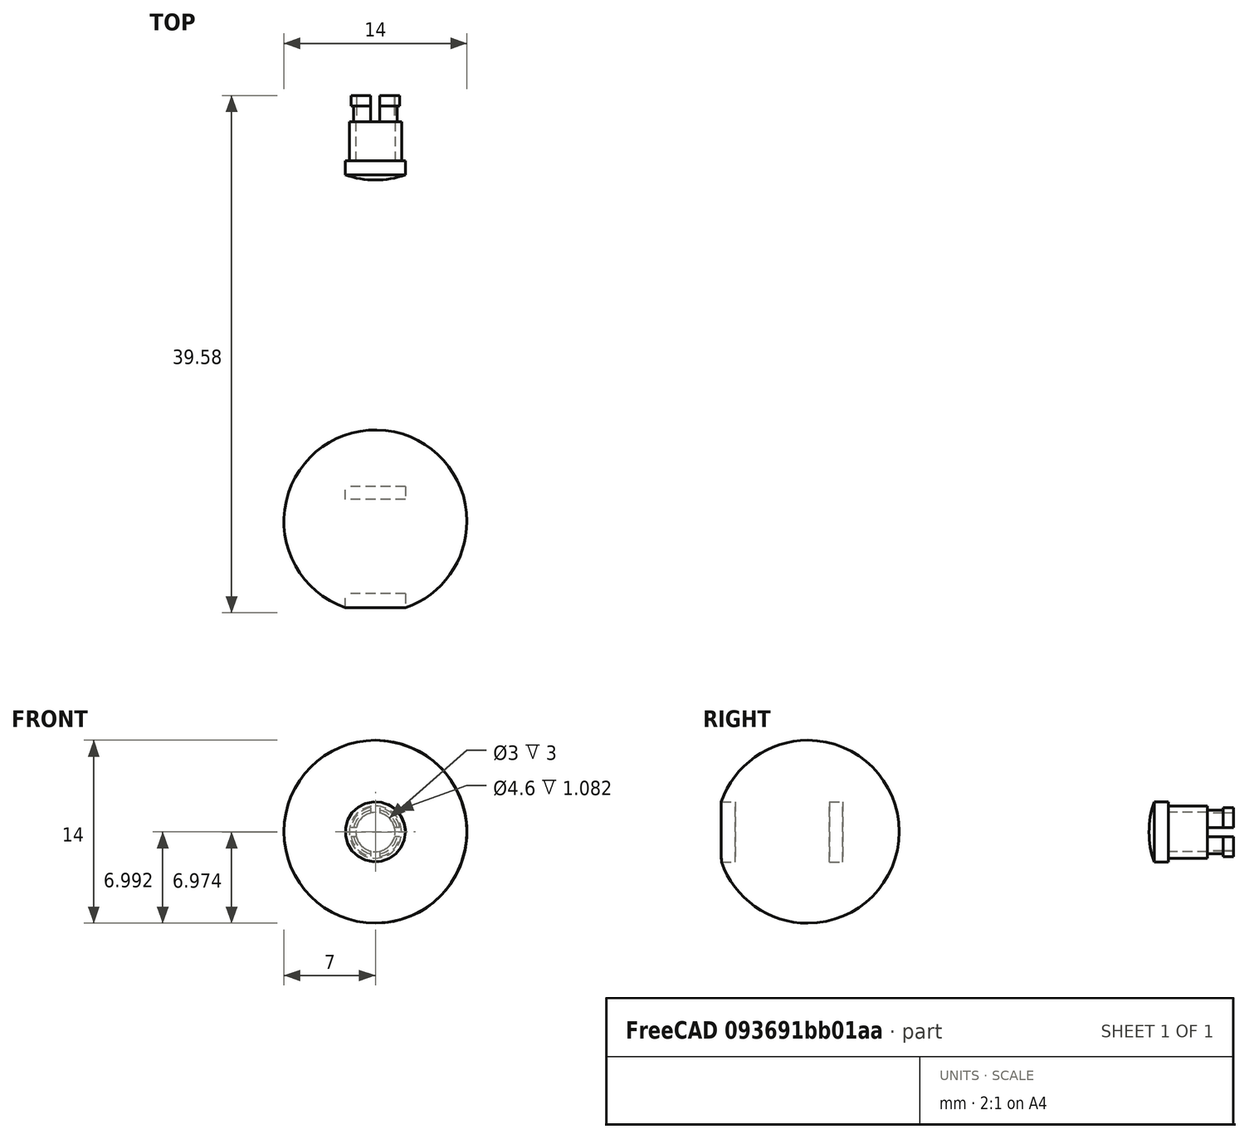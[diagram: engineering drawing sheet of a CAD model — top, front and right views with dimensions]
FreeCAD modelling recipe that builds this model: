
FCSTD DOCUMENT  (FreeCAD 0.21R33771 (Git))
Label: led_lens
License: All rights reserved
LicenseURL: http://en.wikipedia.org/wiki/All_rights_reserved
objects: Part::Cut×5, Part::Box×4, Part::FeaturePython×3, Part::Cylinder×2, Part::MultiFuse×2, Part::Feature×1, Part::Fuse×1, Part::Sphere×1, Part::Common×1
note: 20 computed .brp shape members not serialized (recipe doc carries the construction recipe); baked Part::Feature solids carry a one-line shape summary decoded from their .brp

FEATURE [Part::Feature] Part__Feature468  label="Document"
  Placement = pos=(0,12.544,0) rot=(0,0,1;0rad)
  shape: bbox 3.85 x 5.412 x 4.122 mm, 7 faces, 0 solids (baked)
FEATURE [Part::Cylinder] Cylinder
  Angle = 360
  AttacherType = Attacher::AttachEngine3D
  FirstAngle = 0
  Height = 2
  Placement = pos=(0,-31.287,1.982) rot=(1,0,0;1.5708rad)
  Radius = 2.3
  SecondAngle = 0
FEATURE [Part::FeaturePython] Tube  # WARN: FeaturePython — macro-defined, semantics opaque (R4)
  AttacherType = Attacher::AttachEngine3D
  Height = 3
  InnerRadius = 1.5
  OuterRadius = 2
  Placement = pos=(0,4.834,1.964) rot=(1,0,0;1.5708rad)
FEATURE [Part::FeaturePython] Tube001  # WARN: FeaturePython — macro-defined, semantics opaque (R4)
  AttacherType = Attacher::AttachEngine3D
  Height = 2
  InnerRadius = 1.5
  OuterRadius = 1.7
  Placement = pos=(0,6.835,1.964) rot=(1,0,0;1.5708rad)
FEATURE [Part::Box] Box004  label="Cube004"
  AttacherType = Attacher::AttachEngine3D
  Height = 0.7
  Length = 3
  Placement = pos=(0.326,-0.784,-1.491) rot=(0,1,0;4.71239rad)
  Width = 10
FEATURE [Part::Box] Box005  label="Cube005"
  AttacherType = Attacher::AttachEngine3D
  Height = 0.7
  Length = 3
  Placement = pos=(0,-0.784,1.616) rot=(0,0,1;0rad)
  Width = 10
FEATURE [Part::Box] Box006  label="Cube006"
  AttacherType = Attacher::AttachEngine3D
  Height = 0.7
  Length = 3
  Placement = pos=(-3.072,-0.784,1.616) rot=(0,0,1;0rad)
  Width = 10
FEATURE [Part::Box] Box007  label="Cube007"
  AttacherType = Attacher::AttachEngine3D
  Height = 0.7
  Length = 3
  Placement = pos=(0.326,-0.784,2.677) rot=(0,-1,0;1.5708rad)
  Width = 10
FEATURE [Part::FeaturePython] Tube002  # WARN: FeaturePython — macro-defined, semantics opaque (R4)
  AttacherType = Attacher::AttachEngine3D
  Height = 0.8
  InnerRadius = 1.5
  OuterRadius = 1.9
  Placement = pos=(0,6.835,1.964) rot=(1,0,0;1.5708rad)
FEATURE [Part::Fuse] Fusion
  Base = -> Tube001
  Tool = -> Tube002
FEATURE [Part::Cut] Cut
  Base = -> Fusion
  Tool = -> Box004
FEATURE [Part::Cut] Cut001
  Base = -> Cut
  Tool = -> Box005
FEATURE [Part::Cut] Cut002
  Base = -> Cut001
  Tool = -> Box006
FEATURE [Part::Cut] Cut003
  Base = -> Cut002
  Tool = -> Box007
FEATURE [Part::Cylinder] Cylinder001
  Angle = 360
  AttacherType = Attacher::AttachEngine3D
  FirstAngle = 0
  Height = 1
  Placement = pos=(0,-23.083,1.982) rot=(1,0,0;1.5708rad)
  Radius = 2.3
  SecondAngle = 0
FEATURE [Part::Sphere] Sphere
  Angle1 = -90
  Angle2 = 90
  Angle3 = 360
  AttacherType = Attacher::AttachEngine3D
  Placement = pos=(0,-25.755,1.989) rot=(0,0,1;0rad)
  Radius = 7
FEATURE [Part::Cut] Cut004
  Base = -> Sphere
  Tool = -> Cylinder
FEATURE [Part::Common] Common
  Base = -> Sphere
  Placement = pos=(0,33.12,-0.018) rot=(0,0,1;0rad)
  Tool = -> Cylinder
FEATURE [Part::MultiFuse] Fusion001
  Shapes = -> [Tube,Common]
FEATURE [Part::MultiFuse] Fusion002  label="lens"
  Shapes = -> [Cut003,Fusion001]
